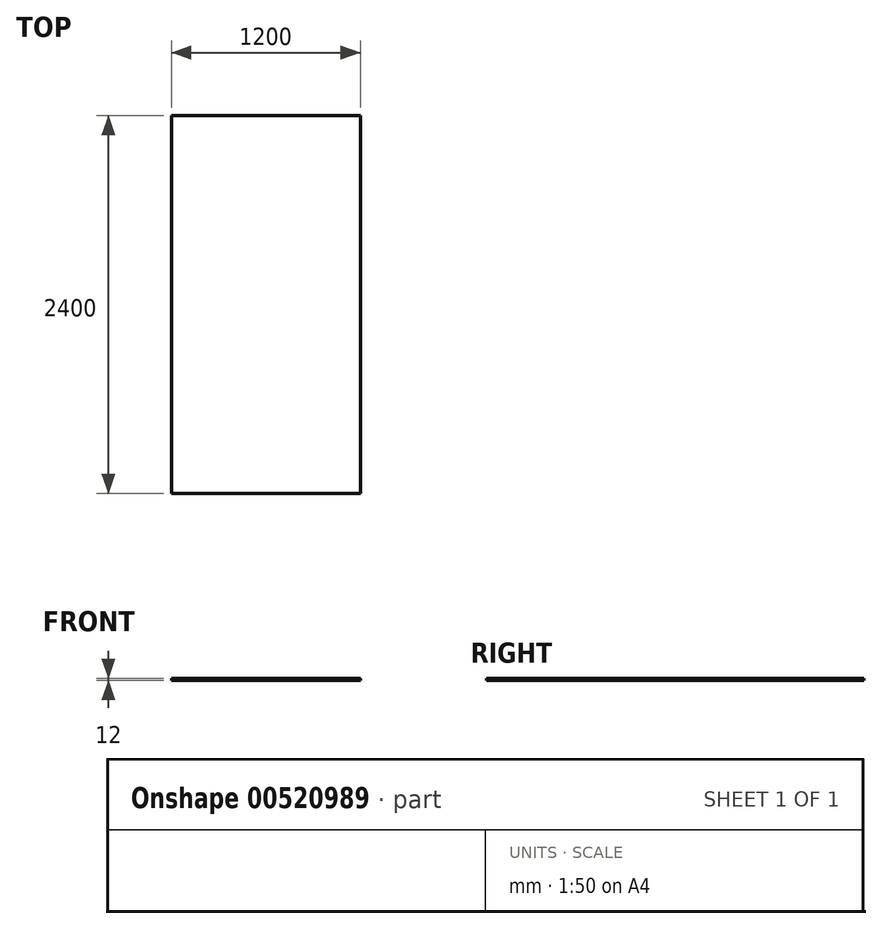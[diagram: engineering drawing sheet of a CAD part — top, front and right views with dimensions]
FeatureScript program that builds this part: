
annotation { "Feature Type Name" : "Feature", "Feature Type Description" : "" }
export const myFeature = defineFeature(function(context is Context, id is Id, definition is map)
    precondition{}
    {
        {
            var Q0;
            Q0=qCreatedBy(makeId("Top.planeOp"),FACE);
            var sketch = newSketch(context, id + "F0", { "sketchPlane" : qUnion([Q0])});
            skLineSegment(sketch, "E0.bottom", {"start": v(-600, 1200) * mm, "end": v(600, 1200) * mm});
            skLineSegment(sketch, "E0.top", {"start": v(-600, -1200) * mm, "end": v(600, -1200) * mm});
            skLineSegment(sketch, "E0.left", {"start": v(-600, 1200) * mm, "end": v(-600, -1200) * mm});
            skLineSegment(sketch, "E0.right", {"start": v(600, 1200) * mm, "end": v(600, -1200) * mm});
            skPoint(sketch, "E0.middle", {"position": v(0, 0) * mm});
            skSolve(sketch);
        }
        {
            var Q0;
            Q0 = qSketchRegion(id + "F0", true);
            extrude(context, id + "F1", {"entities" : qUnion([Q0]), "depth" : 12 * mm, "offsetDistance" : 25 * mm});
        }
    });
